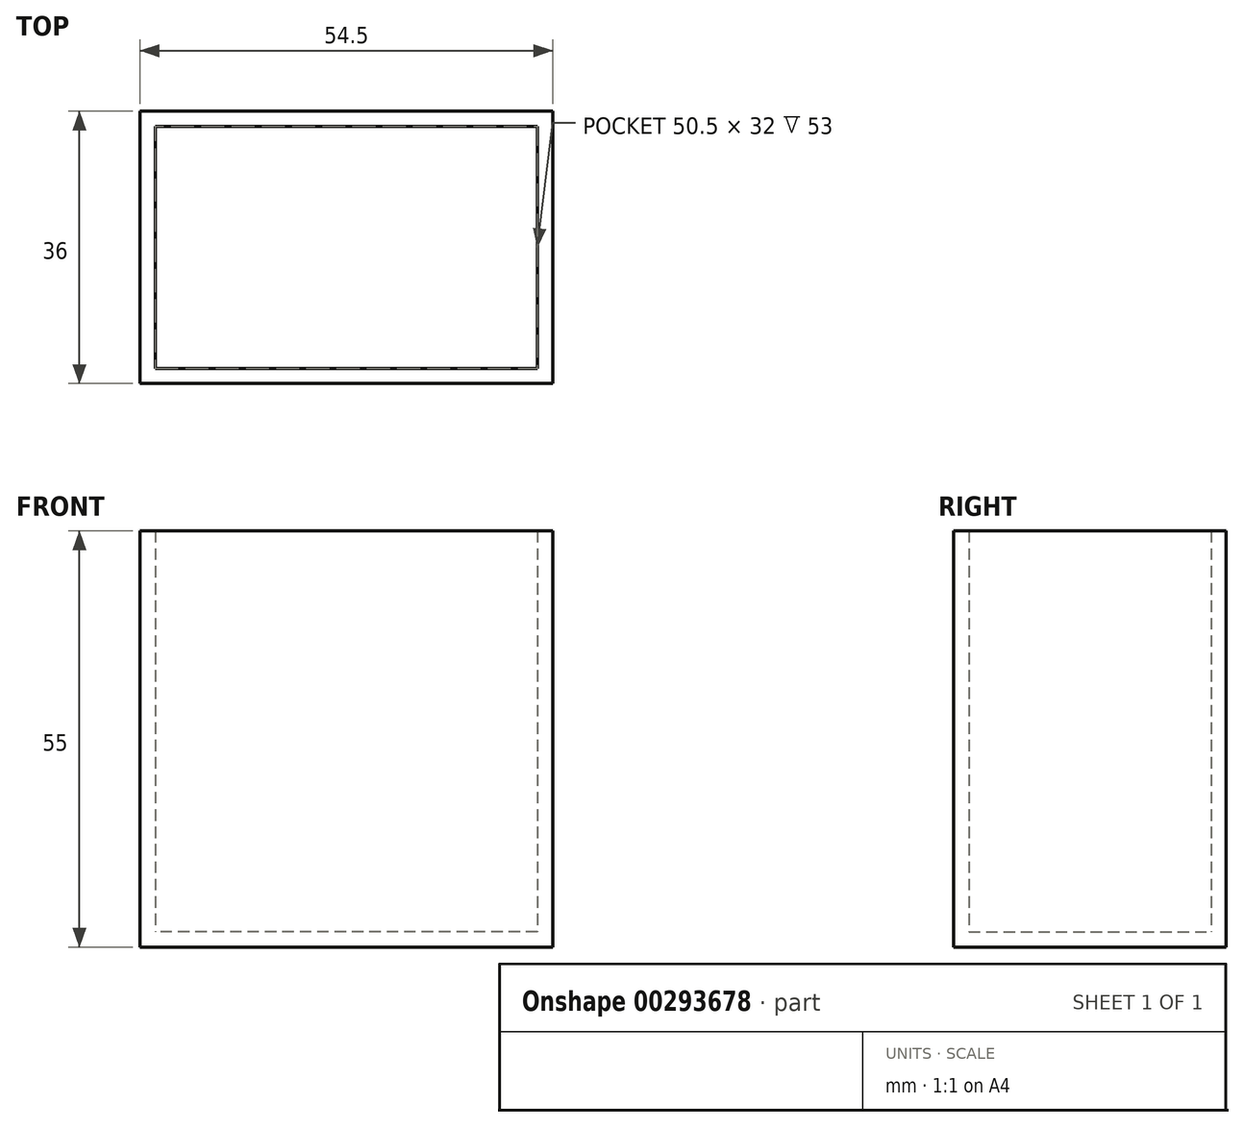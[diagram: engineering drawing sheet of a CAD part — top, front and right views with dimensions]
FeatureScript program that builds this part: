
annotation { "Feature Type Name" : "Feature", "Feature Type Description" : "" }
export const myFeature = defineFeature(function(context is Context, id is Id, definition is map)
    precondition{}
    {
        {
            var Q0;
            Q0=qCreatedBy(makeId("Top.planeOp"),FACE);
            var sketch = newSketch(context, id + "F0", { "sketchPlane" : qUnion([Q0])});
            skLineSegment(sketch, "E0.bottom", {"start": v(25.25, -16) * mm, "end": v(-25.25, -16) * mm});
            skLineSegment(sketch, "E0.top", {"start": v(25.25, 16) * mm, "end": v(-25.25, 16) * mm});
            skLineSegment(sketch, "E0.left", {"start": v(25.25, -16) * mm, "end": v(25.25, 16) * mm});
            skLineSegment(sketch, "E0.right", {"start": v(-25.25, -16) * mm, "end": v(-25.25, 16) * mm});
            skPoint(sketch, "E0.middle", {"position": v(0, 0) * mm});
            skLineSegment(sketch, "E1.0", {"start": v(27.25, 18) * mm, "end": v(-27.25, 18) * mm});
            skLineSegment(sketch, "E1.1", {"start": v(27.25, -18) * mm, "end": v(27.25, 18) * mm});
            skLineSegment(sketch, "E1.2", {"start": v(27.25, -18) * mm, "end": v(-27.25, -18) * mm});
            skLineSegment(sketch, "E1.3", {"start": v(-27.25, -18) * mm, "end": v(-27.25, 18) * mm});
            skSolve(sketch);
        }
        {
            var Q0;
            Q0=makeQuery(id+"F0.imprint","IMPRINT",FACE,{"disambiguationData":[TD([[makeQuery(id+"F0.imprint","IMPRINT",EDGE,{"derivedFrom":sQuery(id+"F0.wireOp",EDGE,"E0.bottom")}),-1.0]])]});
            var Q1;
            Q1=makeQuery(id+"F0.imprint","IMPRINT",FACE,{"disambiguationData":[TD([[makeQuery(id+"F0.imprint","IMPRINT",EDGE,{"derivedFrom":sQuery(id+"F0.wireOp",EDGE,"E0.bottom")}),1.0]])]});
            extrude(context, id + "F1", {"entities" : qUnion([Q0, Q1]), "oppositeDirection" : true, "depth" : 2 * mm});
        }
        {
            var Q0;
            Q0=makeQuery(id+"F0.imprint","IMPRINT",FACE,{"disambiguationData":[TD([[makeQuery(id+"F0.imprint","IMPRINT",EDGE,{"derivedFrom":sQuery(id+"F0.wireOp",EDGE,"E0.bottom")}),1.0]])]});
            extrude(context, id + "F2", {"entities" : qUnion([Q0]), "operationType" : NewBodyOperationType.ADD, "depth" : 53 * mm});
        }
    });
